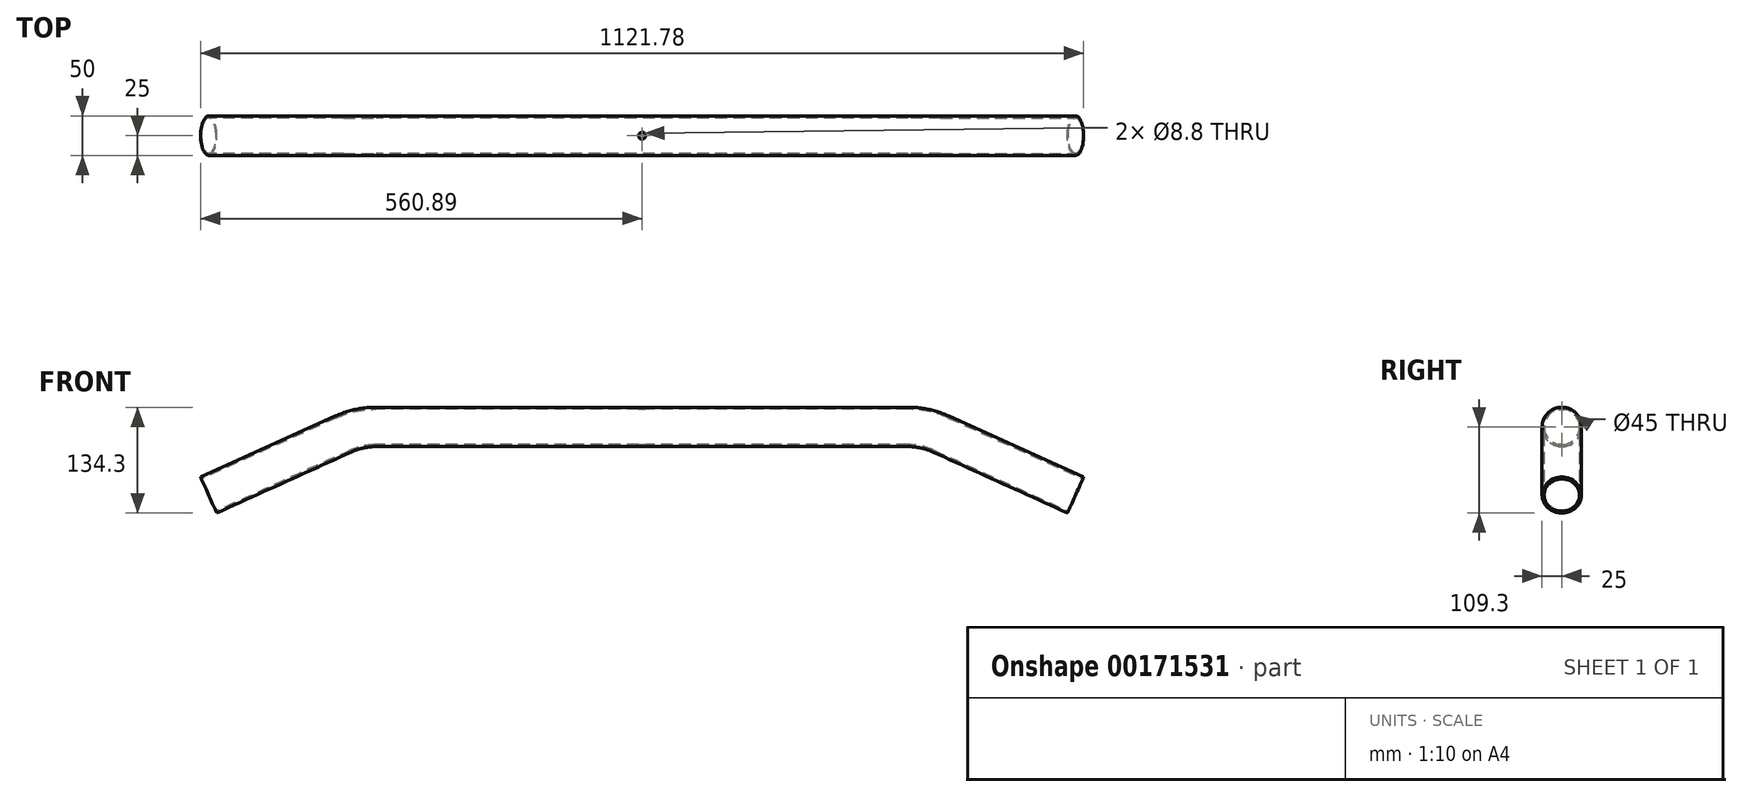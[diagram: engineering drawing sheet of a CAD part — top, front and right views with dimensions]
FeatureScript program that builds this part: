
annotation { "Feature Type Name" : "Feature", "Feature Type Description" : "" }
export const myFeature = defineFeature(function(context is Context, id is Id, definition is map)
    precondition{}
    {
        {
            var Q0;
            Q0=qCreatedBy(makeId("Front.planeOp"),FACE);
            var sketch = newSketch(context, id + "F0", { "sketchPlane" : qUnion([Q0])});
            skLineSegment(sketch, "E0", {"start": v(0, 24.87) * mm, "end": v(-338, 24.87) * mm});
            skLineSegment(sketch, "E1", {"start": v(-389.6, 13.72) * mm, "end": v(-560.83, -63.88) * mm});
            skPoint(sketch, "E2.visualSharp", {"position": v(-365, 24.87) * mm});
            skArc(sketch, "E2.filletArc", {"start": v(-338, 24.87) * mm, "mid": v(-364.4, 22.05) * mm, "end": v(-389.6, 13.72) * mm});
            skSolve(sketch);
        }
        {
            var Q0;
            Q0=qCreatedBy(makeId("Right.planeOp"),FACE);
            var sketch = newSketch(context, id + "F1", { "sketchPlane" : qUnion([Q0])});
            skCircle(sketch, "E3", {"center": v(0, 0) * mm, "radius": 25 * mm});
            skCircle(sketch, "E4", {"center": v(0, 0) * mm, "radius": 22.5 * mm});
            skSolve(sketch);
        }
        {
            var Q0;
            Q0=makeQuery(id+"F1.imprint","IMPRINT",FACE,{"disambiguationData":[TD([[makeQuery(id+"F1.imprint","IMPRINT",EDGE,{"derivedFrom":sQuery(id+"F1.wireOp",EDGE,"E3")}),1.0]])]});
            var Q1;
            Q1=sQuery(id+"F0.wireOp",EDGE,"E0");
            var Q2;
            Q2=sQuery(id+"F0.wireOp",EDGE,"E2.filletArc");
            var Q3;
            Q3=sQuery(id+"F0.wireOp",EDGE,"E1");
            sweep(context, id + "F2", {"profiles" : qUnion([Q0]), "path" : qUnion([Q1, Q2, Q3])});
        }
        {
            var Q0;
            Q0=makeQuery(id+"F2.opSweep","SWEPT_BODY",BODY,{"disambiguationData":[OSD([sQuery(id+"F0.wireOp",EDGE,"E1"),sQuery(id+"F1.wireOp",EDGE,"E3"),sQuery(id+"F1.wireOp",EDGE,"E4")])]});
            var Q1;
            Q1=qCreatedBy(makeId("Right.planeOp"),FACE);
            mirror(context, id + "F3", {"operationType" : NewBodyOperationType.ADD, "entities" : qUnion([Q0]), "mirrorPlane" : qUnion([Q1])});
        }
        {
            var Q0;
            Q0=qCreatedBy(makeId("Top.planeOp"),FACE);
            cPlane(context, id + "F4", {"entities" : qUnion([Q0]), "cplaneType" : CPlaneType.OFFSET, "offset" : 25 * mm, "width" : 150 * mm, "height" : 150 * mm});
        }
        {
            var Q0;
            Q0=qCreatedBy(id+"F4.planeOp",FACE);
            var sketch = newSketch(context, id + "F5", { "sketchPlane" : qUnion([Q0])});
            skPoint(sketch, "E5", {"position": v(0, 0) * mm});
            skSolve(sketch);
        }
        {
            var Q0;
            Q0=sQuery(id+"F5.wireOp",VERTEX,"E5");
            var Q1;
            Q1=makeQuery(id+"F2.opSweep","SWEPT_BODY",BODY,{"disambiguationData":[OSD([sQuery(id+"F0.wireOp",EDGE,"E1"),sQuery(id+"F1.wireOp",EDGE,"E3"),sQuery(id+"F1.wireOp",EDGE,"E4")])]});
            hole(context, id + "F6", {"style" : HoleStyle.SIMPLE, "endStyle" : HoleEndStyle.THROUGH, "standardTappedOrClearance" : lookupTablePath({ "standard" : "ISO", "fit" : "Normal", "size" : "M8", "type" : "Clearance" }), "standardBlindInLast" : lookupTablePath({ "fit" : "Standard", "standard" : "ISO", "size" : "M8", "type" : "Clearance" }), "holeDiameter" : 8.8 * mm, "locations" : qUnion([Q0]), "scope" : qUnion([Q1]), "isTappedThrough" : true});
        }
    });
